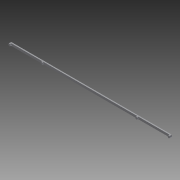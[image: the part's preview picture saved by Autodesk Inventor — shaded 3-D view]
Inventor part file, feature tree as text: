
AUTODESK INVENTOR PART (.ipt)
format: ipt  version: 2011 (Build 150239000, 239)  size: 93,184 bytes
history: native  units: in
note: dims shown in document units (in); Inventor stores cm internally (conversion verified against a paired STEP export)
features: extrude x4, sketch x4
ambient origin geometry x8: Origin, YZ Plane, XZ Plane, XY Plane, X Axis, Y Axis, Z Axis, Center Point
bodies: Solid1 (feature_tree)
feature tree (8):
  extrude  "Extrusion1"  Depth=0.25in
  extrude  "Extrusion2"  Depth=0.125in
  extrude  "Extrusion3"  Depth=3.531in
  extrude  "Extrusion4"  Depth=0.125in TaperAngle=0.0deg
  sketch  "Sketch1"  dims[d0=17.469in d1=0.25in]
  sketch  "Sketch2"  dims[d2=0.125in d3=0.0in d4=0.125in]
  sketch  "Sketch3"  dims[d5=3.531in d6=3.531in]
  sketch  "Sketch4"  dims[d7=0.125in d8=0.0in d9=0.125in d10=0.0in d11=0.125in d12=0.0in]
